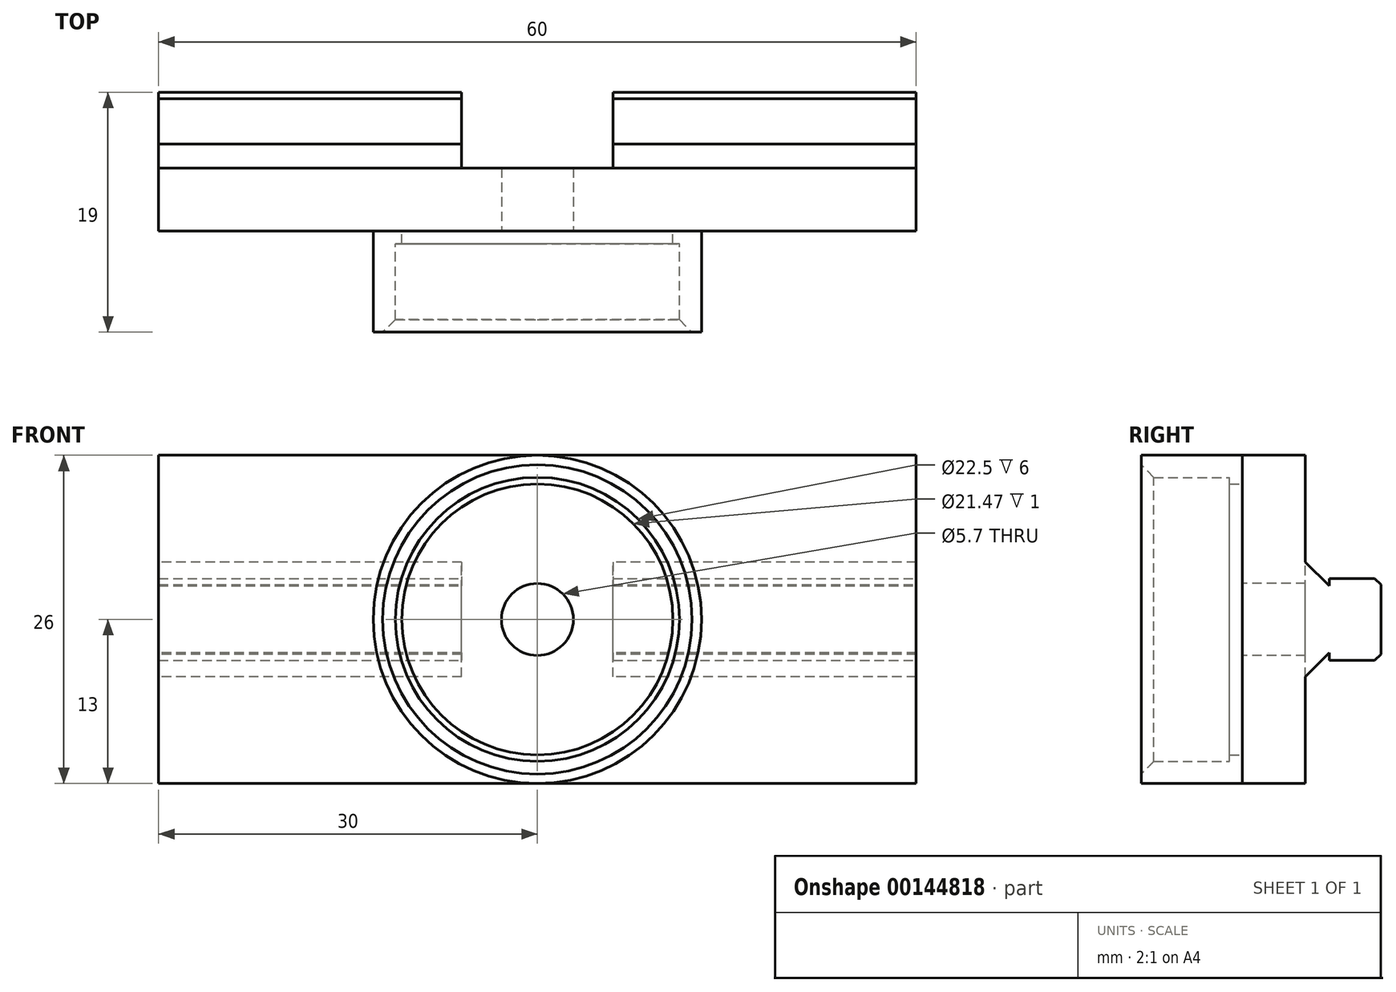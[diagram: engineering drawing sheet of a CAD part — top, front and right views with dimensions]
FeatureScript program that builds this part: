
annotation { "Feature Type Name" : "Feature", "Feature Type Description" : "" }
export const myFeature = defineFeature(function(context is Context, id is Id, definition is map)
    precondition{}
    {
        {
            var Q0;
            Q0=qCreatedBy(makeId("Front.planeOp"),FACE);
            var sketch = newSketch(context, id + "F0", { "sketchPlane" : qUnion([Q0])});
            skLineSegment(sketch, "E0.bottom", {"start": v(30, 13) * mm, "end": v(-30, 13) * mm});
            skLineSegment(sketch, "E0.top", {"start": v(30, -13) * mm, "end": v(-30, -13) * mm});
            skLineSegment(sketch, "E0.left", {"start": v(30, 13) * mm, "end": v(30, -13) * mm});
            skLineSegment(sketch, "E0.right", {"start": v(-30, 13) * mm, "end": v(-30, -13) * mm});
            skPoint(sketch, "E0.middle", {"position": v(0, 0) * mm});
            skSolve(sketch);
        }
        {
            var Q0;
            Q0 = qSketchRegion(id + "F0", true);
            extrude(context, id + "F1", {"entities" : qUnion([Q0]), "depth" : 5 * mm});
        }
        {
            var Q0;
            Q0=makeQuery(id+"F1.opExtrude","CAP_FACE",FACE,{"disambiguationData":[OSD([sQuery(id+"F0.wireOp",EDGE,"E0.bottom"),sQuery(id+"F0.wireOp",EDGE,"E0.top"),sQuery(id+"F0.wireOp",EDGE,"E0.left"),sQuery(id+"F0.wireOp",EDGE,"E0.right")])],"isStart":false});
            var sketch = newSketch(context, id + "F2", { "sketchPlane" : qUnion([Q0])});
            skCircle(sketch, "E1", {"center": v(0, 0) * mm, "radius": 13 * mm});
            skCircle(sketch, "E2", {"center": v(0, 0) * mm, "radius": 11.25 * mm});
            skCircle(sketch, "E3", {"center": v(0, 0) * mm, "radius": 10.75 * mm});
            skSolve(sketch);
        }
        {
            var Q0;
            Q0=makeQuery(id+"F2.imprint","IMPRINT",FACE,{"disambiguationData":[TD([[makeQuery(id+"F2.imprint","IMPRINT",EDGE,{"derivedFrom":sQuery(id+"F2.wireOp",EDGE,"E2")}),-1.0]])]});
            extrude(context, id + "F3", {"entities" : qUnion([Q0]), "operationType" : NewBodyOperationType.ADD, "depth" : 8 * mm});
        }
        {
            var Q0;
            Q0=makeQuery(id+"F3.boolean.opBoolean","SPLIT",FACE,{"disambiguationData":[TD([makeQuery(id+"F3.opExtrude","SWEPT_FACE",FACE,{"disambiguationData":[OSD([sQuery(id+"F2.wireOp",EDGE,"E2")])]})])],"derivedFrom":makeQuery(id+"F1.opExtrude","CAP_FACE",FACE,{"disambiguationData":[OSD([sQuery(id+"F0.wireOp",EDGE,"E0.bottom"),sQuery(id+"F0.wireOp",EDGE,"E0.top"),sQuery(id+"F0.wireOp",EDGE,"E0.left"),sQuery(id+"F0.wireOp",EDGE,"E0.right")])],"isStart":false})});
            var sketch = newSketch(context, id + "F4", { "sketchPlane" : qUnion([Q0])});
            skCircle(sketch, "E4", {"center": v(0, 0) * mm, "radius": 10.73 * mm});
            skSolve(sketch);
        }
        {
            var Q0;
            Q0=makeQuery(id+"F4.imprint","IMPRINT",FACE,{"disambiguationData":[TD([[makeQuery(id+"F4.imprint","IMPRINT",EDGE,{"derivedFrom":sQuery(id+"F4.wireOp",EDGE,"E4")}),-1.0]])]});
            extrude(context, id + "F5", {"entities" : qUnion([Q0]), "operationType" : NewBodyOperationType.ADD, "depth" : 1 * mm});
        }
        {
            var Q0;
            Q0=makeQuery(id+"F3.opExtrude","CAP_EDGE",EDGE,{"disambiguationData":[OSD([sQuery(id+"F2.wireOp",EDGE,"E2")])],"isStart":false});
            chamfer(context, id + "F6", {"entities" : qUnion([Q0]), "width" : 1 * mm, "tangentPropagation" : true});
        }
        {
            var Q0;
            Q0=makeQuery(id+"F1.opExtrude","CAP_FACE",FACE,{"disambiguationData":[OSD([sQuery(id+"F0.wireOp",EDGE,"E0.bottom"),sQuery(id+"F0.wireOp",EDGE,"E0.top"),sQuery(id+"F0.wireOp",EDGE,"E0.left"),sQuery(id+"F0.wireOp",EDGE,"E0.right")])],"isStart":true});
            var sketch = newSketch(context, id + "F7", { "sketchPlane" : qUnion([Q0])});
            skLineSegment(sketch, "E5.bottom", {"start": v(30, -4.65) * mm, "end": v(-30, -4.65) * mm});
            skLineSegment(sketch, "E5.top", {"start": v(30, 4.65) * mm, "end": v(-30, 4.65) * mm});
            skLineSegment(sketch, "E5.left", {"start": v(30, -4.65) * mm, "end": v(30, 4.65) * mm});
            skLineSegment(sketch, "E5.right", {"start": v(-30, -4.65) * mm, "end": v(-30, 4.65) * mm});
            skPoint(sketch, "E5.middle", {"position": v(0, 0) * mm});
            skSolve(sketch);
        }
        {
            var Q0;
            Q0 = qSketchRegion(id + "F7", true);
            extrude(context, id + "F8", {"entities" : qUnion([Q0]), "operationType" : NewBodyOperationType.ADD, "depth" : 1.9 * mm});
        }
        {
            var Q0;
            Q0=makeQuery(id+"F8.opExtrude","CAP_EDGE",EDGE,{"disambiguationData":[OSD([sQuery(id+"F7.wireOp",EDGE,"E5.top")])],"isStart":false});
            var Q1;
            Q1=makeQuery(id+"F8.opExtrude","CAP_EDGE",EDGE,{"disambiguationData":[OSD([sQuery(id+"F7.wireOp",EDGE,"E5.bottom")])],"isStart":false});
            chamfer(context, id + "F9", {"entities" : qUnion([Q0, Q1]), "width" : 2 * mm, "tangentPropagation" : true});
        }
        {
            var Q0;
            Q0=makeQuery(id+"F8.opExtrude","CAP_FACE",FACE,{"disambiguationData":[OSD([sQuery(id+"F7.wireOp",EDGE,"E5.bottom"),sQuery(id+"F7.wireOp",EDGE,"E5.top"),sQuery(id+"F7.wireOp",EDGE,"E5.left"),sQuery(id+"F7.wireOp",EDGE,"E5.right")])],"isStart":false});
            var sketch = newSketch(context, id + "F10", { "sketchPlane" : qUnion([Q0])});
            skLineSegment(sketch, "E6.bottom", {"start": v(30, -3.25) * mm, "end": v(-30, -3.25) * mm});
            skLineSegment(sketch, "E6.top", {"start": v(30, 3.25) * mm, "end": v(-30, 3.25) * mm});
            skLineSegment(sketch, "E6.left", {"start": v(30, -3.25) * mm, "end": v(30, 3.25) * mm});
            skLineSegment(sketch, "E6.right", {"start": v(-30, -3.25) * mm, "end": v(-30, 3.25) * mm});
            skPoint(sketch, "E6.middle", {"position": v(0, 0) * mm});
            skSolve(sketch);
        }
        {
            var Q0;
            Q0 = qSketchRegion(id + "F10", true);
            extrude(context, id + "F11", {"entities" : qUnion([Q0]), "operationType" : NewBodyOperationType.ADD, "depth" : 4.1 * mm});
        }
        {
            var Q0;
            Q0=makeQuery(id+"F11.opExtrude","CAP_EDGE",EDGE,{"disambiguationData":[OSD([sQuery(id+"F10.wireOp",EDGE,"E6.top")])],"isStart":false});
            var Q1;
            Q1=makeQuery(id+"F11.opExtrude","CAP_EDGE",EDGE,{"disambiguationData":[OSD([sQuery(id+"F10.wireOp",EDGE,"E6.bottom")])],"isStart":false});
            chamfer(context, id + "F12", {"entities" : qUnion([Q0, Q1]), "width" : 0.5 * mm, "tangentPropagation" : true});
        }
        {
            var Q0;
            Q0=qCreatedBy(makeId("Front.planeOp"),FACE);
            var sketch = newSketch(context, id + "F13", { "sketchPlane" : qUnion([Q0])});
            skCircle(sketch, "E7", {"center": v(0, 0) * mm, "radius": 2.85 * mm});
            skSolve(sketch);
        }
        {
            var Q0;
            Q0 = qSketchRegion(id + "F13", true);
            extrude(context, id + "F14", {"entities" : qUnion([Q0]), "operationType" : NewBodyOperationType.REMOVE, "endBound" : BoundingType.SYMMETRIC, "oppositeDirection" : true, "depth" : 25 * mm});
        }
        {
            var Q0;
            Q0=qCreatedBy(makeId("Top.planeOp"),FACE);
            var sketch = newSketch(context, id + "F15", { "sketchPlane" : qUnion([Q0])});
            skLineSegment(sketch, "E8.bottom", {"start": v(0, 0) * mm, "end": v(6, 0) * mm});
            skLineSegment(sketch, "E8.top", {"start": v(0, 6) * mm, "end": v(6, 6) * mm});
            skLineSegment(sketch, "E8.left", {"start": v(0, 0) * mm, "end": v(0, 6) * mm});
            skLineSegment(sketch, "E8.right", {"start": v(6, 0) * mm, "end": v(6, 6) * mm});
            skLineSegment(sketch, "E9.bottom", {"start": v(0, 0) * mm, "end": v(-6, 0) * mm});
            skLineSegment(sketch, "E9.top", {"start": v(0, 6) * mm, "end": v(-6, 6) * mm});
            skLineSegment(sketch, "E9.right", {"start": v(-6, 0) * mm, "end": v(-6, 6) * mm});
            skSolve(sketch);
        }
        {
            var Q0;
            Q0 = qSketchRegion(id + "F15", true);
            extrude(context, id + "F16", {"entities" : qUnion([Q0]), "operationType" : NewBodyOperationType.REMOVE, "endBound" : BoundingType.SYMMETRIC, "oppositeDirection" : true, "depth" : 25 * mm});
        }
    });
